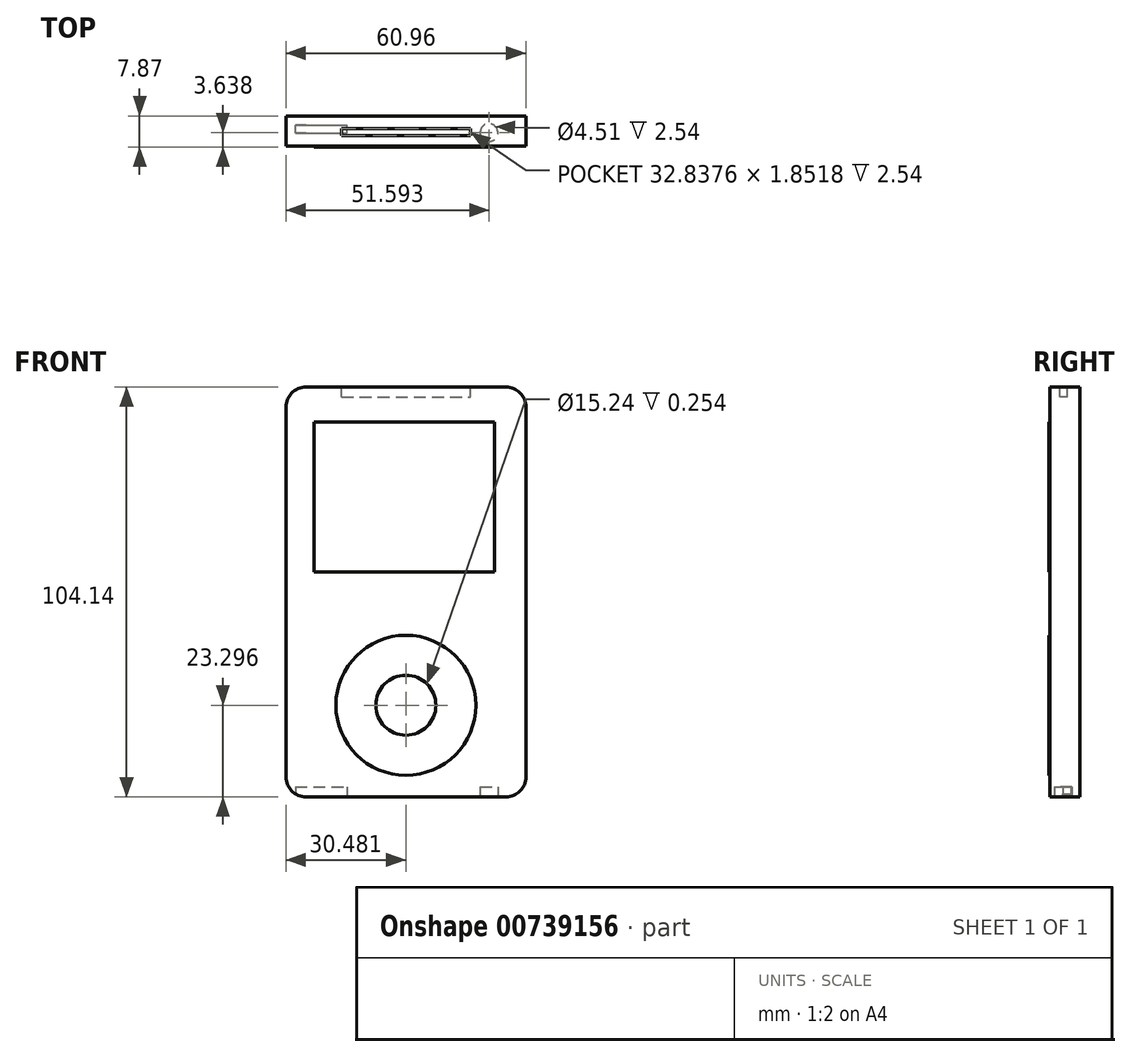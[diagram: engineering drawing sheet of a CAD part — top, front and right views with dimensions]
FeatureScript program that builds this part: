
annotation { "Feature Type Name" : "Feature", "Feature Type Description" : "" }
export const myFeature = defineFeature(function(context is Context, id is Id, definition is map)
    precondition{}
    {
        {
            var Q0;
            Q0=qCreatedBy(makeId("Front.planeOp"),FACE);
            var sketch = newSketch(context, id + "F0", { "sketchPlane" : qUnion([Q0])});
            skLineSegment(sketch, "E0", {"start": v(-53.28, 55.3) * mm, "end": v(7.68, 55.3) * mm});
            skLineSegment(sketch, "E1", {"start": v(7.68, 55.3) * mm, "end": v(7.68, -48.84) * mm});
            skLineSegment(sketch, "E2", {"start": v(7.68, -48.84) * mm, "end": v(-53.28, -48.84) * mm});
            skLineSegment(sketch, "E3", {"start": v(-53.28, -48.84) * mm, "end": v(-53.28, 55.3) * mm});
            skSolve(sketch);
        }
        {
            var Q0;
            Q0 = qSketchRegion(id + "F0", true);
            extrude(context, id + "F1", {"entities" : qUnion([Q0]), "depth" : 7.62 * mm, "offsetDistance" : 25.4 * mm});
        }
        {
            var Q0;
            Q0=makeQuery(id+"F1.opExtrude","CAP_FACE",FACE,{"disambiguationData":[OSD([sQuery(id+"F0.wireOp",EDGE,"E0"),sQuery(id+"F0.wireOp",EDGE,"E1"),sQuery(id+"F0.wireOp",EDGE,"E2"),sQuery(id+"F0.wireOp",EDGE,"E3")])],"isStart":false});
            var sketch = newSketch(context, id + "F2", { "sketchPlane" : qUnion([Q0])});
            skLineSegment(sketch, "E4.bottom", {"start": v(-46.15, 46.4) * mm, "end": v(-0.24, 46.4) * mm});
            skLineSegment(sketch, "E4.top", {"start": v(-46.15, 8.3) * mm, "end": v(-0.24, 8.3) * mm});
            skLineSegment(sketch, "E4.left", {"start": v(-46.15, 46.4) * mm, "end": v(-46.15, 8.3) * mm});
            skLineSegment(sketch, "E4.right", {"start": v(-0.24, 46.4) * mm, "end": v(-0.24, 8.3) * mm});
            skCircle(sketch, "E5", {"center": v(-22.8, -25.54) * mm, "radius": 17.78 * mm});
            skCircle(sketch, "E6", {"center": v(-22.8, -25.54) * mm, "radius": 7.62 * mm});
            skSolve(sketch);
        }
        {
            var Q0;
            Q0 = qSketchRegion(id + "F2", true);
            extrude(context, id + "F3", {"entities" : qUnion([Q0]), "operationType" : NewBodyOperationType.ADD, "depth" : 0.25 * mm, "offsetDistance" : 25.4 * mm});
        }
        {
            var Q0;
            Q0=makeQuery(id+"F1.opExtrude","SWEPT_FACE",FACE,{"disambiguationData":[OSD([sQuery(id+"F0.wireOp",EDGE,"E2")])]});
            var sketch = newSketch(context, id + "F4", { "sketchPlane" : qUnion([Q0])});
            skLineSegment(sketch, "E7.bottom", {"start": v(-50.88, 4.3) * mm, "end": v(-37.8, 4.3) * mm});
            skLineSegment(sketch, "E7.top", {"start": v(-50.88, 2.33) * mm, "end": v(-37.8, 2.33) * mm});
            skLineSegment(sketch, "E7.left", {"start": v(-50.88, 4.3) * mm, "end": v(-50.88, 2.33) * mm});
            skLineSegment(sketch, "E7.right", {"start": v(-37.8, 4.3) * mm, "end": v(-37.8, 2.33) * mm});
            skSolve(sketch);
        }
        {
            var Q0;
            Q0 = qSketchRegion(id + "F4", true);
            extrude(context, id + "F5", {"entities" : qUnion([Q0]), "operationType" : NewBodyOperationType.REMOVE, "oppositeDirection" : true, "depth" : 2.54 * mm, "offsetDistance" : 25.4 * mm});
        }
        {
            var Q0;
            Q0=makeQuery(id+"F1.opExtrude","SWEPT_FACE",FACE,{"disambiguationData":[OSD([sQuery(id+"F0.wireOp",EDGE,"E2")])]});
            var sketch = newSketch(context, id + "F6", { "sketchPlane" : qUnion([Q0])});
            skCircle(sketch, "E8", {"center": v(-1.69, 4.23) * mm, "radius": 2.25 * mm});
            skSolve(sketch);
        }
        {
            var Q0;
            Q0 = qSketchRegion(id + "F6", true);
            extrude(context, id + "F7", {"entities" : qUnion([Q0]), "operationType" : NewBodyOperationType.REMOVE, "oppositeDirection" : true, "depth" : 2.54 * mm, "offsetDistance" : 25.4 * mm});
        }
        {
            var Q0;
            Q0=makeQuery(id+"F1.opExtrude","SWEPT_EDGE",EDGE,{"disambiguationData":[OSD([sQuery(id+"F0.wireOp",EDGE,"E0"),sQuery(id+"F0.wireOp",EDGE,"E1")])]});
            var Q1;
            Q1=makeQuery(id+"F1.opExtrude","SWEPT_EDGE",EDGE,{"disambiguationData":[OSD([sQuery(id+"F0.wireOp",EDGE,"E0"),sQuery(id+"F0.wireOp",EDGE,"E3")])]});
            var Q2;
            Q2=makeQuery(id+"F1.opExtrude","SWEPT_EDGE",EDGE,{"disambiguationData":[OSD([sQuery(id+"F0.wireOp",EDGE,"E1"),sQuery(id+"F0.wireOp",EDGE,"E2")])]});
            var Q3;
            Q3=makeQuery(id+"F1.opExtrude","SWEPT_EDGE",EDGE,{"disambiguationData":[OSD([sQuery(id+"F0.wireOp",EDGE,"E2"),sQuery(id+"F0.wireOp",EDGE,"E3")])]});
            fillet(context, id + "F8", {"entities" : qUnion([Q0, Q1, Q2, Q3]), "radius" : 5.08 * mm, "tangentPropagation" : true, "allowEdgeOverflow" : false});
        }
        {
            var Q0;
            Q0=makeQuery(id+"F1.opExtrude","SWEPT_FACE",FACE,{"disambiguationData":[OSD([sQuery(id+"F0.wireOp",EDGE,"E0")])]});
            var sketch = newSketch(context, id + "F9", { "sketchPlane" : qUnion([Q0])});
            skLineSegment(sketch, "E9.bottom", {"start": v(-39.16, -3.18) * mm, "end": v(-6.32, -3.18) * mm});
            skLineSegment(sketch, "E9.top", {"start": v(-39.16, -5.03) * mm, "end": v(-6.32, -5.03) * mm});
            skLineSegment(sketch, "E9.left", {"start": v(-39.16, -3.18) * mm, "end": v(-39.16, -5.03) * mm});
            skLineSegment(sketch, "E9.right", {"start": v(-6.32, -3.18) * mm, "end": v(-6.32, -5.03) * mm});
            skSolve(sketch);
        }
        {
            var Q0;
            Q0 = qSketchRegion(id + "F9", true);
            extrude(context, id + "F10", {"entities" : qUnion([Q0]), "operationType" : NewBodyOperationType.REMOVE, "oppositeDirection" : true, "depth" : 2.54 * mm, "offsetDistance" : 25.4 * mm});
        }
    });
